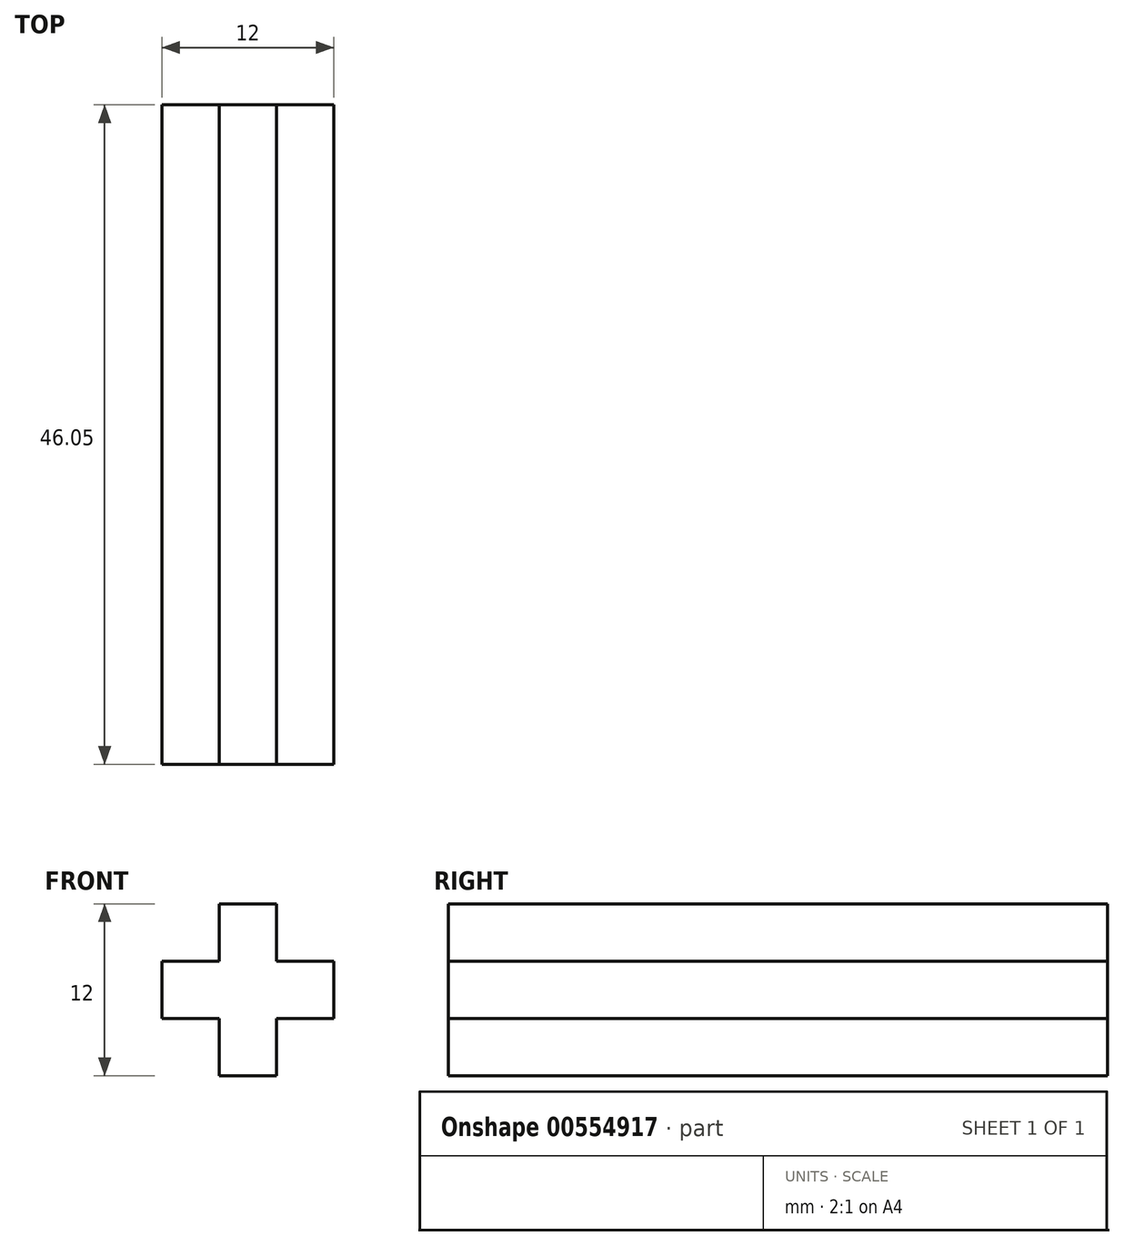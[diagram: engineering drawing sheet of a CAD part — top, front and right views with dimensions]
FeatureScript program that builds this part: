
annotation { "Feature Type Name" : "Feature", "Feature Type Description" : "" }
export const myFeature = defineFeature(function(context is Context, id is Id, definition is map)
    precondition{}
    {
        {
            var Q0;
            Q0=qCreatedBy(makeId("Front.planeOp"),FACE);
            var sketch = newSketch(context, id + "F0", { "sketchPlane" : qUnion([Q0])});
            skLineSegment(sketch, "E0", {"start": v(-0.99, 4) * mm, "end": v(3.01, 4) * mm});
            skLineSegment(sketch, "E1", {"start": v(3.01, 4) * mm, "end": v(3.01, 0) * mm});
            skLineSegment(sketch, "E2", {"start": v(7.01, 0) * mm, "end": v(7.01, -4) * mm});
            skLineSegment(sketch, "E3", {"start": v(7.01, -4) * mm, "end": v(3.01, -4) * mm});
            skLineSegment(sketch, "E4", {"start": v(3.01, -4) * mm, "end": v(3.01, -8) * mm});
            skLineSegment(sketch, "E5", {"start": v(3.01, -8) * mm, "end": v(-0.99, -8) * mm});
            skLineSegment(sketch, "E6", {"start": v(-0.99, -8) * mm, "end": v(-0.99, -4) * mm});
            skLineSegment(sketch, "E7", {"start": v(-0.99, -4) * mm, "end": v(-4.99, -4) * mm});
            skLineSegment(sketch, "E8", {"start": v(-4.99, -4) * mm, "end": v(-4.99, 0) * mm});
            skLineSegment(sketch, "E9", {"start": v(-4.99, 0) * mm, "end": v(-0.99, 0) * mm});
            skLineSegment(sketch, "E10", {"start": v(-0.99, 0) * mm, "end": v(-0.99, 4) * mm});
            skLineSegment(sketch, "E11", {"start": v(3.01, 0) * mm, "end": v(7.01, 0) * mm});
            skSolve(sketch);
        }
        {
            var Q0;
            Q0=makeQuery(id+"F0.imprint","IMPRINT",FACE,{"disambiguationData":[TD([[makeQuery(id+"F0.imprint","IMPRINT",EDGE,{"derivedFrom":sQuery(id+"F0.wireOp",EDGE,"E0")}),-1.0]])]});
            extrude(context, id + "F1", {"entities" : qUnion([Q0]), "depth" : 46.05 * mm, "offsetDistance" : 25.4 * mm});
        }
    });
